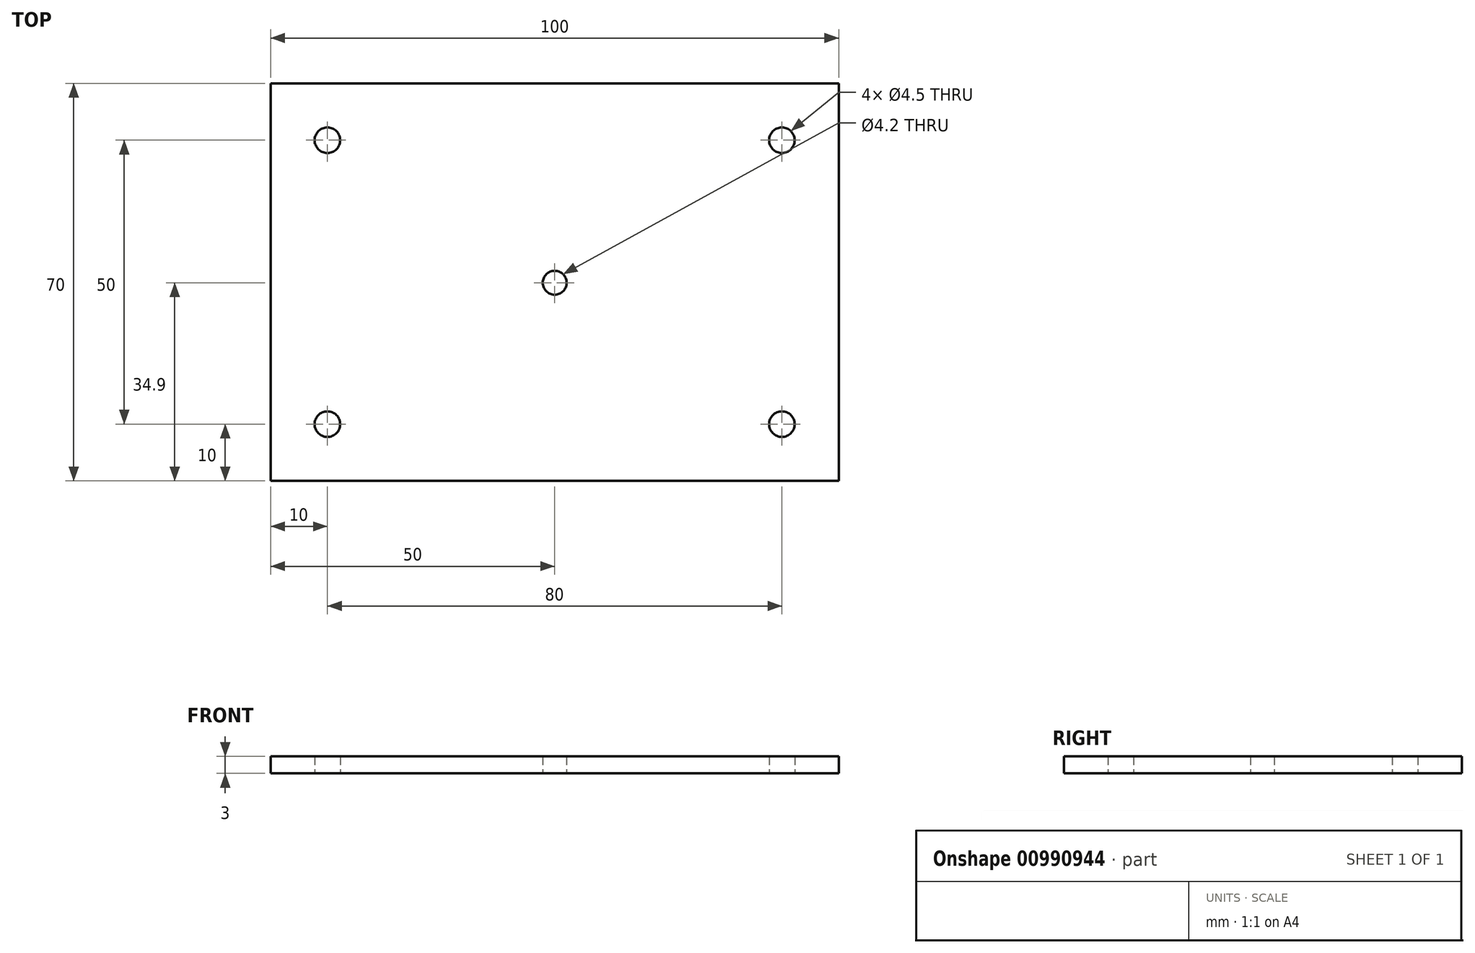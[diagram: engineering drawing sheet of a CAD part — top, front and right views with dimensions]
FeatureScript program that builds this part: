
annotation { "Feature Type Name" : "Feature", "Feature Type Description" : "" }
export const myFeature = defineFeature(function(context is Context, id is Id, definition is map)
    precondition{}
    {
        {
            var Q0;
            Q0=qCreatedBy(makeId("Top.planeOp"),FACE);
            var sketch = newSketch(context, id + "F0", { "sketchPlane" : qUnion([Q0])});
            skLineSegment(sketch, "E0.bottom", {"start": v(50, -34.9) * mm, "end": v(-50, -34.9) * mm});
            skLineSegment(sketch, "E0.left", {"start": v(50, -34.9) * mm, "end": v(50, 35.1) * mm});
            skLineSegment(sketch, "E0.right", {"start": v(-50, -34.9) * mm, "end": v(-50, 35.1) * mm});
            skLineSegment(sketch, "E1", {"start": v(-50, 35.1) * mm, "end": v(50, 35.1) * mm});
            skLineSegment(sketch, "E2", {"start": v(-50, -24.9) * mm, "end": v(50, -24.9) * mm, "construction": true});
            skLineSegment(sketch, "E3", {"start": v(-40, 35.1) * mm, "end": v(-40, -34.9) * mm, "construction": true});
            skLineSegment(sketch, "E4", {"start": v(40, 35.1) * mm, "end": v(40, -34.9) * mm, "construction": true});
            skPoint(sketch, "E5", {"position": v(-50, 0.1) * mm});
            skLineSegment(sketch, "E6", {"start": v(-50, 35.1) * mm, "end": v(-50, -34.9) * mm});
            skLineSegment(sketch, "E7", {"start": v(-50, 0.1) * mm, "end": v(50, 0.1) * mm, "construction": true});
            skLineSegment(sketch, "E8", {"start": v(-50, 25.1) * mm, "end": v(50, 25.1) * mm, "construction": true});
            skCircle(sketch, "E9", {"center": v(-40, 25.1) * mm, "radius": 2.25 * mm});
            skCircle(sketch, "E10.MirrorC", {"center": v(40, 25.1) * mm, "radius": 2.25 * mm});
            skCircle(sketch, "E11.MirrorC", {"center": v(-40, -24.9) * mm, "radius": 2.25 * mm});
            skCircle(sketch, "E12.MirrorC", {"center": v(40, -24.9) * mm, "radius": 2.25 * mm});
            skPoint(sketch, "E13", {"position": v(-40, 35.1) * mm});
            skCircle(sketch, "E14", {"center": v(0, 0) * mm, "radius": 2.1 * mm});
            skPoint(sketch, "E15.orphan", {"position": v(-50, 45.1) * mm});
            skPoint(sketch, "E16.start.orphan", {"position": v(-40, 45.1) * mm});
            skSolve(sketch);
        }
        {
            var Q0;
            {var subQ4=sQuery(id+"F0.wireOp",EDGE,"E0.bottom");Q0=makeQuery(id+"F0.imprint","IMPRINT",FACE,{"disambiguationData":[TD([[makeQuery(id+"F0.imprint","IMPRINT",EDGE,{"derivedFrom":subQ4}),-1.0]])]});}
            var Q1;
            {var subQ0=sQuery(id+"F0.wireOp",EDGE,"1c6f4ef4-dcee-4795-916a-16c6468b9974.trimOffspring");Q1=makeQuery(id+"F0.imprint","IMPRINT",FACE,{"disambiguationData":[TD([[makeQuery(id+"F0.imprint","IMPRINT",EDGE,{"derivedFrom":subQ0}),1.0]])]});}
            extrude(context, id + "F1", {"entities" : qUnion([Q0, Q1]), "depth" : 3 * mm, "offsetDistance" : 25 * mm});
        }
    });
